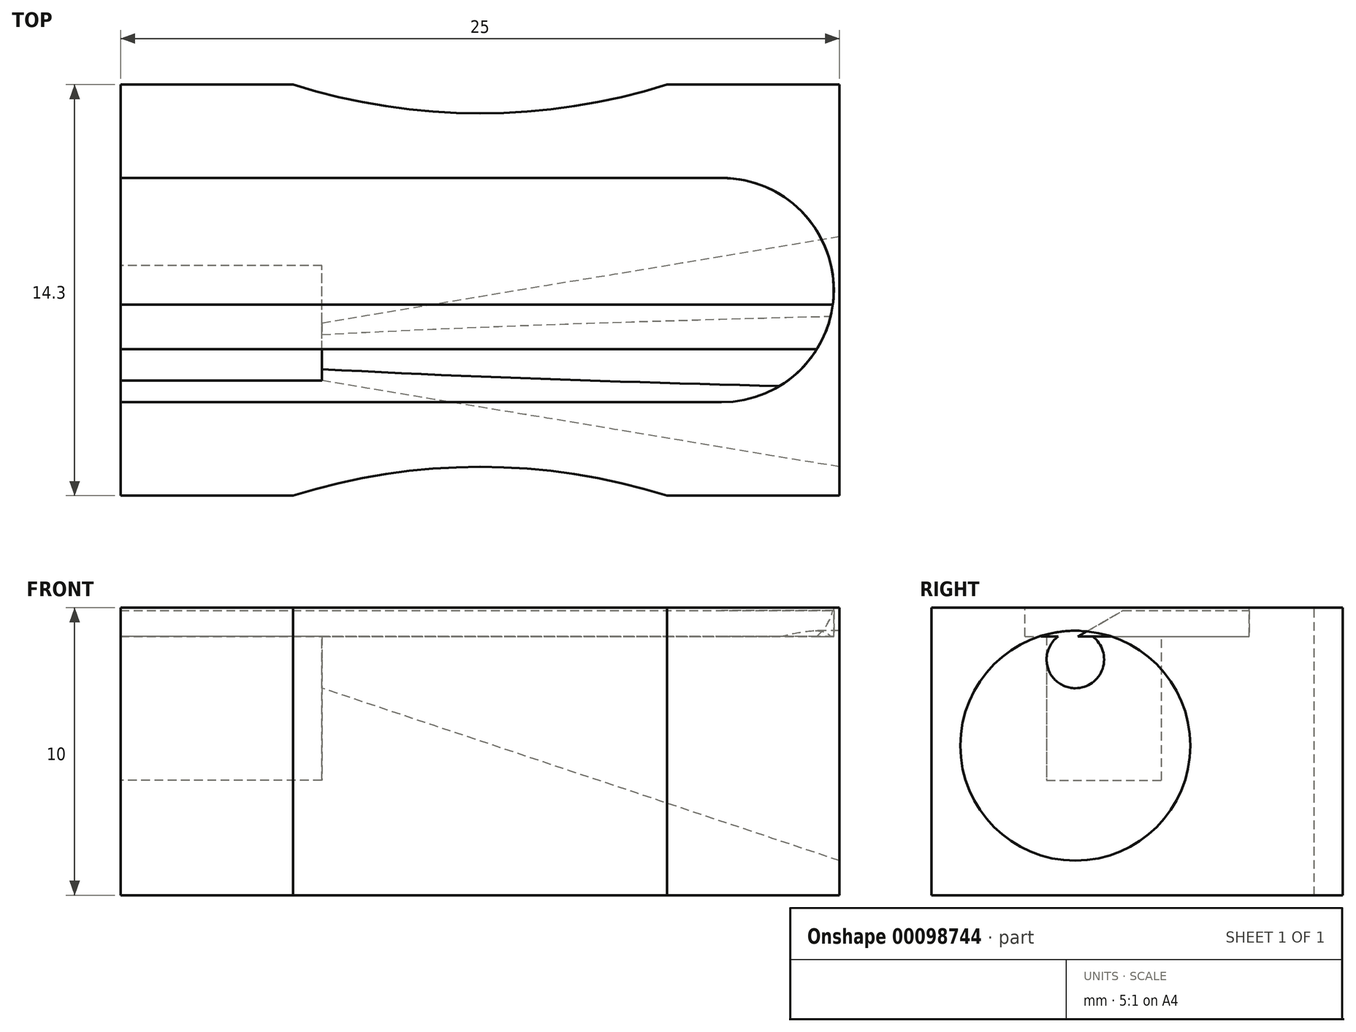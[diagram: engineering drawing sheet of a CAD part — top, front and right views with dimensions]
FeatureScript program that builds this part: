
annotation { "Feature Type Name" : "Feature", "Feature Type Description" : "" }
export const myFeature = defineFeature(function(context is Context, id is Id, definition is map)
    precondition{}
    {
        {
            var Q0;
            Q0=qCreatedBy(makeId("Front.planeOp"),FACE);
            var sketch = newSketch(context, id + "F0", { "sketchPlane" : qUnion([Q0])});
            skLineSegment(sketch, "E0", {"start": v(0, 0) * mm, "end": v(-25, 0) * mm});
            skLineSegment(sketch, "E1", {"start": v(-25, 0) * mm, "end": v(-25, 10) * mm});
            skLineSegment(sketch, "E2", {"start": v(-25, 10) * mm, "end": v(0, 10) * mm});
            skLineSegment(sketch, "E3", {"start": v(0, 10) * mm, "end": v(0, 0) * mm});
            skSolve(sketch);
        }
        {
            var Q0;
            Q0 = qSketchRegion(id + "F0", true);
            extrude(context, id + "F1", {"entities" : qUnion([Q0]), "depth" : 14.3 * mm});
        }
        {
            var Q0;
            Q0=qCreatedBy(makeId("Right.planeOp"),FACE);
            cPlane(context, id + "F2", {"entities" : qUnion([Q0]), "cplaneType" : CPlaneType.OFFSET, "offset" : 18 * mm, "oppositeDirection" : true, "width" : 150 * mm, "height" : 150 * mm});
        }
        {
            var Q0;
            Q0=makeQuery(id+"F1.opExtrude","SWEPT_FACE",FACE,{"disambiguationData":[OSD([sQuery(id+"F0.wireOp",EDGE,"E3")])]});
            var sketch = newSketch(context, id + "F3", { "sketchPlane" : qUnion([Q0])});
            skCircle(sketch, "E4", {"center": v(-9.3, 5.2) * mm, "radius": 4 * mm});
            skSolve(sketch);
        }
        {
            var Q0;
            Q0=qCreatedBy(id+"F2.planeOp",FACE);
            var sketch = newSketch(context, id + "F4", { "sketchPlane" : qUnion([Q0])});
            skCircle(sketch, "E5", {"center": v(-9.3, 8.2) * mm, "radius": 1 * mm});
            skSolve(sketch);
        }
        {
            var Q0;
            Q0 = qSketchRegion(id + "F3", true);
            var Q1;
            Q1 = qSketchRegion(id + "F4", true);
            var Q2;
            Q2=sQuery(id+"F3.wireOp",EDGE,"E4");
            var Q3;
            Q3=sQuery(id+"F4.wireOp",EDGE,"E5");
            loft(context, id + "F5", {"operationType" : NewBodyOperationType.REMOVE, "sheetProfilesArray" : [{ "sheetProfileEntities" : qUnion([Q0]) }, { "sheetProfileEntities" : qUnion([Q1]) }], "wireProfilesArray" : [{ "wireProfileEntities" : qUnion([Q2]) }, { "wireProfileEntities" : qUnion([Q3]) }]});
        }
        {
            var Q0;
            Q0=makeQuery(id+"F1.opExtrude","SWEPT_FACE",FACE,{"disambiguationData":[OSD([sQuery(id+"F0.wireOp",EDGE,"E1")])]});
            var sketch = newSketch(context, id + "F6", { "sketchPlane" : qUnion([Q0])});
            skLineSegment(sketch, "E6", {"start": v(10.3, 10) * mm, "end": v(10.3, 4) * mm});
            skLineSegment(sketch, "E7", {"start": v(10.3, 4) * mm, "end": v(6.3, 4) * mm});
            skLineSegment(sketch, "E8", {"start": v(6.3, 4) * mm, "end": v(6.3, 10) * mm});
            skLineSegment(sketch, "E9", {"start": v(6.3, 10) * mm, "end": v(10.3, 10) * mm});
            skSolve(sketch);
        }
        {
            var Q0;
            Q0 = qSketchRegion(id + "F6", true);
            extrude(context, id + "F7", {"entities" : qUnion([Q0]), "operationType" : NewBodyOperationType.REMOVE, "oppositeDirection" : true, "depth" : 7 * mm});
        }
        {
            var Q0;
            Q0=makeQuery(id+"F1.opExtrude","SWEPT_FACE",FACE,{"disambiguationData":[OSD([sQuery(id+"F0.wireOp",EDGE,"E2")])]});
            var sketch = newSketch(context, id + "F8", { "sketchPlane" : qUnion([Q0])});
            skLineSegment(sketch, "E10", {"start": v(0, -7.15) * mm, "end": v(-25, -7.15) * mm, "construction": true});
            skLineSegment(sketch, "E11", {"start": v(-25, -3.25) * mm, "end": v(-25, -6.3) * mm});
            skLineSegment(sketch, "E12", {"start": v(-25, -6.3) * mm, "end": v(-18, -6.3) * mm});
            skLineSegment(sketch, "E13", {"start": v(-18, -6.3) * mm, "end": v(-18, -10.3) * mm});
            skLineSegment(sketch, "E14", {"start": v(-18, -10.3) * mm, "end": v(-25, -10.3) * mm});
            skLineSegment(sketch, "E15", {"start": v(-25, -10.3) * mm, "end": v(-25, -11.05) * mm});
            skLineSegment(sketch, "E16", {"start": v(-25, -3.25) * mm, "end": v(-4.1, -3.25) * mm});
            skLineSegment(sketch, "E17", {"start": v(-25, -11.05) * mm, "end": v(-4.1, -11.05) * mm});
            skArc(sketch, "E18", {"start": v(-4.1, -3.25) * mm, "mid": v(-0.2, -7.15) * mm, "end": v(-4.1, -11.05) * mm});
            skSolve(sketch);
        }
        {
            var Q0;
            Q0=makeQuery(id+"F1.opExtrude","SWEPT_FACE",FACE,{"disambiguationData":[OSD([sQuery(id+"F0.wireOp",EDGE,"E2")])]});
            var sketch = newSketch(context, id + "F9", { "sketchPlane" : qUnion([Q0])});
            skLineSegment(sketch, "E19", {"start": v(-6, -14.3) * mm, "end": v(-19, -14.3) * mm});
            skLineSegment(sketch, "E20", {"start": v(-6, 0) * mm, "end": v(-19, 0) * mm});
            skPoint(sketch, "E21", {"position": v(-12.5, -14.3) * mm});
            skPoint(sketch, "E22", {"position": v(-12.5, 0) * mm});
            skLineSegment(sketch, "E23", {"start": v(-12.5, 0) * mm, "end": v(-12.5, -1) * mm, "construction": true});
            skLineSegment(sketch, "E24", {"start": v(-12.5, -14.3) * mm, "end": v(-12.5, -13.3) * mm, "construction": true});
            skArc(sketch, "E25", {"start": v(-19, 0) * mm, "mid": v(-12.5, -1) * mm, "end": v(-6, 0) * mm});
            skArc(sketch, "E26", {"start": v(-6, -14.3) * mm, "mid": v(-12.5, -13.3) * mm, "end": v(-19, -14.3) * mm});
            skSolve(sketch);
        }
        {
            var Q0;
            Q0 = qSketchRegion(id + "F9", true);
            extrude(context, id + "F10", {"entities" : qUnion([Q0]), "operationType" : NewBodyOperationType.REMOVE, "oppositeDirection" : true, "depth" : 10 * mm});
        }
        {
            var Q0;
            Q0 = qSketchRegion(id + "F8", true);
            extrude(context, id + "F11", {"entities" : qUnion([Q0]), "operationType" : NewBodyOperationType.REMOVE, "oppositeDirection" : true, "depth" : 1 * mm});
        }
        {
            var Q0;
            {var subQ0=sQuery(id+"F6.wireOp",EDGE,"E8");var subQ1=sQuery(id+"F8.wireOp",EDGE,"E16");var subQ2=sQuery(id+"F8.wireOp",EDGE,"E18");Q0=makeQuery(id+"F11.boolean.opBoolean","COPY",FACE,{"disambiguationData":[TD([makeQuery(id+"F7.boolean.opBoolean","COPY",FACE,{"derivedFrom":makeQuery(id+"F7.opExtrude","SWEPT_FACE",FACE,{"disambiguationData":[OSD([subQ0])]})})])],"derivedFrom":makeQuery(id+"F11.opExtrude","CAP_FACE",FACE,{"disambiguationData":[OSD([sQuery(id+"F8.wireOp",EDGE,"E11"),sQuery(id+"F8.wireOp",EDGE,"E12"),sQuery(id+"F8.wireOp",EDGE,"E13"),sQuery(id+"F8.wireOp",EDGE,"E14"),sQuery(id+"F8.wireOp",EDGE,"E15"),subQ1,sQuery(id+"F8.wireOp",EDGE,"E17"),subQ2])],"isStart":false})});}
            var sketch = newSketch(context, id + "F12", { "sketchPlane" : qUnion([Q0])});
            skLineSegment(sketch, "E27", {"start": v(-25, -3.25) * mm, "end": v(-4.1, -3.25) * mm});
            skLineSegment(sketch, "E28", {"start": v(-25, -3.25) * mm, "end": v(-25, -9.25) * mm});
            skLineSegment(sketch, "E29", {"start": v(-4.1, -3.25) * mm, "end": v(-4.1, -11.05) * mm, "construction": true});
            skLineSegment(sketch, "E30", {"start": v(-25, -9.25) * mm, "end": v(-4.1, -9.25) * mm});
            skPoint(sketch, "E31", {"position": v(-4.1, -7.15) * mm});
            skArc(sketch, "E32", {"start": v(-0.81, -9.25) * mm, "mid": v(-0.68, -5.28) * mm, "end": v(-4.1, -3.25) * mm});
            skLineSegment(sketch, "E33", {"start": v(-4.1, -9.25) * mm, "end": v(-0.81, -9.25) * mm});
            skSolve(sketch);
        }
        {
            var Q0;
            Q0 = qSketchRegion(id + "F12", true);
            extrude(context, id + "F13", {"entities" : qUnion([Q0]), "depth" : 0.9 * mm});
        }
        {
            var Q0;
            Q0=makeQuery(id+"F13.opExtrude","CAP_EDGE",EDGE,{"disambiguationData":[OSD([sQuery(id+"F12.wireOp",EDGE,"E30"),sQuery(id+"F12.wireOp",EDGE,"E33")])],"isStart":false});
            chamfer(context, id + "F14", {"entities" : qUnion([Q0]), "chamferType" : ChamferType.OFFSET_ANGLE, "width" : 1.6 * mm, "oppositeDirection" : false, "angle" : 30 * degree, "tangentPropagation" : true});
        }
    });
